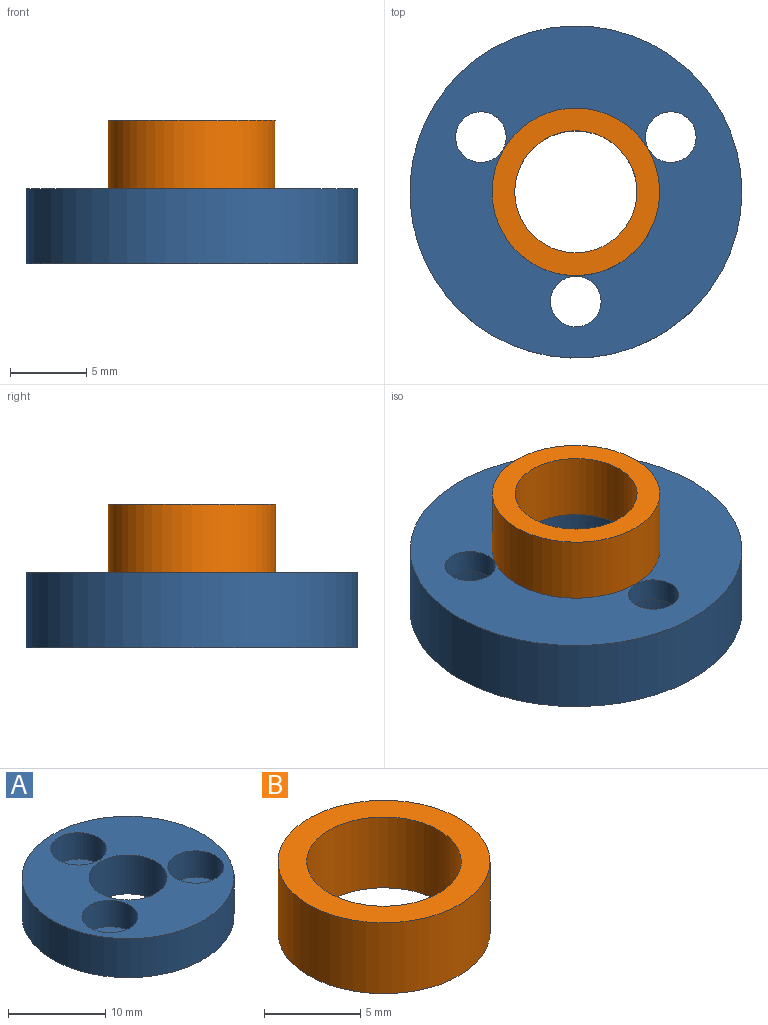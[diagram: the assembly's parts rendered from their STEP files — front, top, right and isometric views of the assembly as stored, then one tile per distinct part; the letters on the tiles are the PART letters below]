
ASSEMBLY  parts=2 mates=1
PART A: 13 faces, bbox 21.8x21.8x4.9 mm
  f0: cylinder r=1.66mm len=3.32mm, axis (0,0,1), area 16.7mm2, adj f5,f10
  f1: cylinder r=1.66mm len=3.32mm, axis (0,0,1), area 16.7mm2, adj f5,f12
  f2: cylinder r=1.66mm len=3.32mm, axis (0,0,1), area 16.7mm2, adj f5,f8
  f3: cylinder r=10.9mm len=21.8mm, axis (0,0,1), area 335.6mm2, adj f5,f6
  f4: cylinder r=4.01mm len=8.02mm, axis (0,0,1), area 123.4mm2, adj f5,f6
  f5: plane 21.8x21.8mm, normal (0,0,-1), area 296.8mm2, adj f0,f1,f2,f3,f4
  f6: plane 21.8x21.8mm, normal (0,0,1), area 244.9mm2, adj f3,f4,f7,f9,f11
  f7: cylinder r=2.88mm len=5.75mm, axis (0,0,1), area 59.6mm2, adj f6,f8
  f8: plane 5.75x5.75mm, normal (0,0,1), area 17.3mm2, adj f2,f7
  f9: cylinder r=2.88mm len=5.75mm, axis (0,0,1), area 59.6mm2, adj f6,f10
  f10: plane 5.75x5.75mm, normal (0,0,1), area 17.3mm2, adj f0,f9
  f11: cylinder r=2.88mm len=5.75mm, axis (0,0,1), area 59.6mm2, adj f6,f12
  f12: plane 5.75x5.75mm, normal (0,0,1), area 17.3mm2, adj f1,f11
PART B: 4 faces, bbox 11x11x4.5 mm
  f0: cylinder r=4.01mm len=8.02mm, axis (0,0,1), area 113.3mm2, adj f2,f3
  f1: cylinder r=5.5mm len=11mm, axis (0,0,1), area 155.5mm2, adj f2,f3
  f2: plane 11x11mm, normal (0,0,-1), area 44.6mm2, adj f0,f1
  f3: plane 11x11mm, normal (0,0,1), area 44.6mm2, adj f0,f1
PLACE A rot(axis=(1,0,0),180deg) t=(-2.76,-9.54,-6.6)mm
PLACE B t=(-2.76,-9.54,7.7)mm
MATE fastened A.f4 <-> B.f0  axis (0,0,1) through (-2.76,-9.54,-1.7)mm
